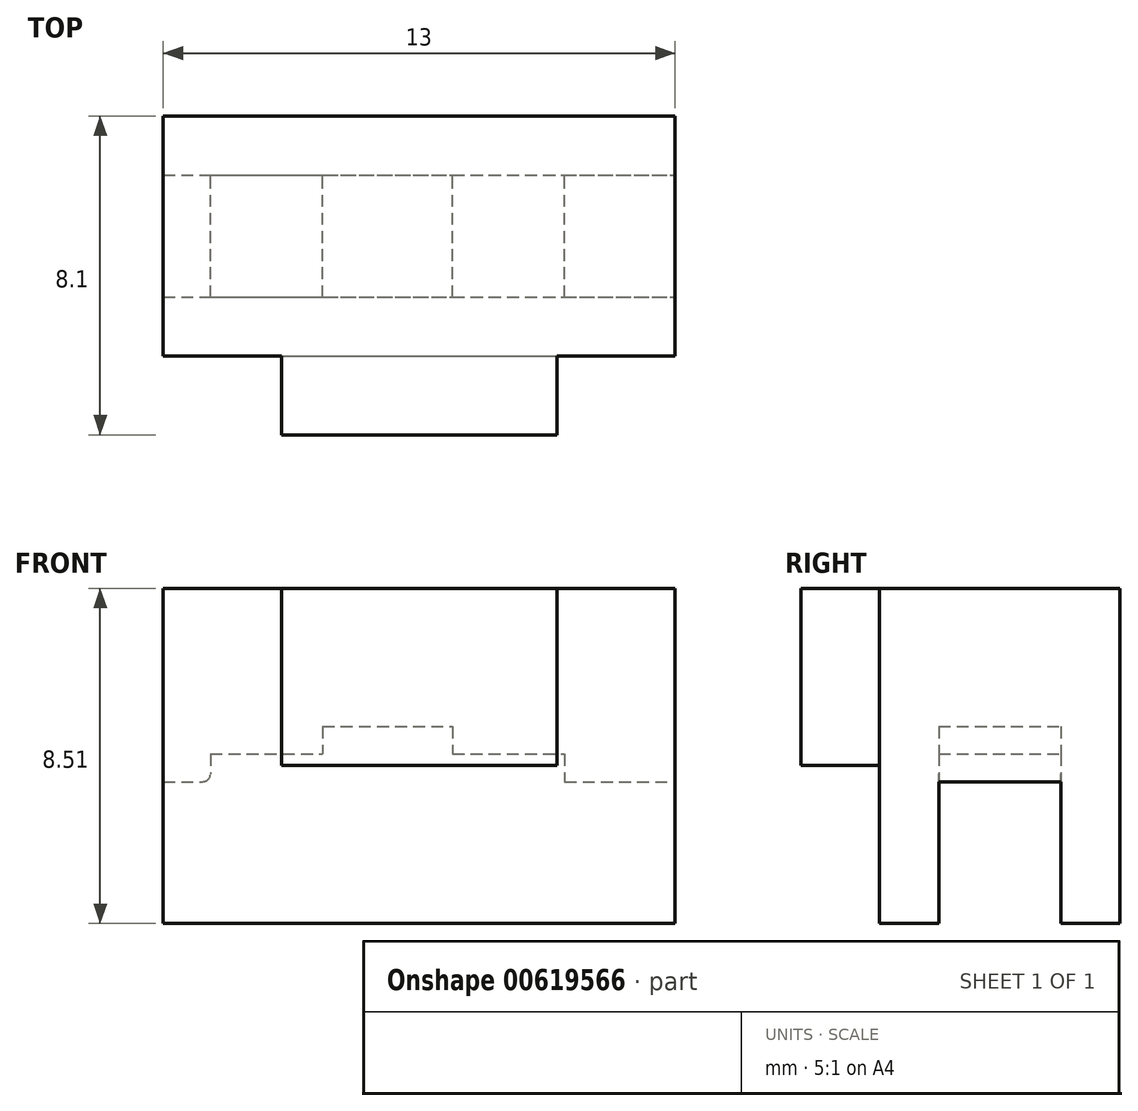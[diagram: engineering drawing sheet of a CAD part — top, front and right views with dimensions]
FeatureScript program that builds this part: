
annotation { "Feature Type Name" : "Feature", "Feature Type Description" : "" }
export const myFeature = defineFeature(function(context is Context, id is Id, definition is map)
    precondition{}
    {
        {
            var Q0;
            Q0=qCreatedBy(makeId("Top.planeOp"),FACE);
            var sketch = newSketch(context, id + "F0", { "sketchPlane" : qUnion([Q0])});
            skLineSegment(sketch, "E0.bottom", {"start": v(-6.5, 3.05) * mm, "end": v(6.5, 3.05) * mm});
            skLineSegment(sketch, "E0.top", {"start": v(-6.5, 1.55) * mm, "end": v(6.5, 1.55) * mm});
            skLineSegment(sketch, "E0.left", {"start": v(-6.5, 3.05) * mm, "end": v(-6.5, 1.55) * mm});
            skLineSegment(sketch, "E0.right", {"start": v(6.5, 3.05) * mm, "end": v(6.5, 1.55) * mm});
            skLineSegment(sketch, "E1.MirrorCS", {"start": v(6.5, -3.05) * mm, "end": v(6.5, -1.55) * mm});
            skLineSegment(sketch, "E2.MirrorCS", {"start": v(-6.5, -3.05) * mm, "end": v(-6.5, -1.55) * mm});
            skLineSegment(sketch, "E3.MirrorCS", {"start": v(-6.5, -3.05) * mm, "end": v(6.5, -3.05) * mm});
            skLineSegment(sketch, "E4.MirrorCS", {"start": v(-6.5, -1.55) * mm, "end": v(6.5, -1.55) * mm});
            skSolve(sketch);
        }
        {
            var Q0;
            Q0 = qSketchRegion(id + "F0", true);
            extrude(context, id + "F1", {"entities" : qUnion([Q0]), "oppositeDirection" : true, "depth" : 3.6 * mm, "offsetDistance" : 25 * mm});
        }
        {
            var Q0;
            Q0=qCreatedBy(makeId("Top.planeOp"),FACE);
            var sketch = newSketch(context, id + "F2", { "sketchPlane" : qUnion([Q0])});
            skLineSegment(sketch, "E5.bottom", {"start": v(-6.5, 3.05) * mm, "end": v(6.5, 3.05) * mm});
            skLineSegment(sketch, "E5.top", {"start": v(-6.5, -3.05) * mm, "end": v(6.5, -3.05) * mm});
            skLineSegment(sketch, "E5.left", {"start": v(-6.5, 3.05) * mm, "end": v(-6.5, -3.05) * mm});
            skLineSegment(sketch, "E5.right", {"start": v(6.5, 3.05) * mm, "end": v(6.5, -3.05) * mm});
            skSolve(sketch);
        }
        {
            var Q0;
            Q0 = qSketchRegion(id + "F2", true);
            extrude(context, id + "F3", {"entities" : qUnion([Q0]), "operationType" : NewBodyOperationType.ADD, "depth" : 4.9 * mm, "offsetDistance" : 25 * mm});
        }
        {
            var Q0;
            Q0=makeQuery(id+"F3.opExtrude","CAP_FACE",FACE,{"disambiguationData":[OSD([sQuery(id+"F2.wireOp",EDGE,"E5.bottom"),sQuery(id+"F2.wireOp",EDGE,"E5.top"),sQuery(id+"F2.wireOp",EDGE,"E5.left"),sQuery(id+"F2.wireOp",EDGE,"E5.right")])],"isStart":true});
            var sketch = newSketch(context, id + "F4", { "sketchPlane" : qUnion([Q0])});
            skLineSegment(sketch, "E6.bottom", {"start": v(-5.3, 1.55) * mm, "end": v(3.7, 1.55) * mm});
            skLineSegment(sketch, "E6.top", {"start": v(-5.3, -1.55) * mm, "end": v(3.7, -1.55) * mm});
            skLineSegment(sketch, "E6.left", {"start": v(-5.3, 1.55) * mm, "end": v(-5.3, -1.55) * mm});
            skLineSegment(sketch, "E6.right", {"start": v(3.7, 1.55) * mm, "end": v(3.7, -1.55) * mm});
            skSolve(sketch);
        }
        {
            var Q0;
            Q0=makeQuery(id+"F4.imprint","IMPRINT",FACE,{"disambiguationData":[TD([[makeQuery(id+"F4.imprint","IMPRINT",EDGE,{"derivedFrom":sQuery(id+"F4.wireOp",EDGE,"E6.bottom")}),-1.0]])]});
            extrude(context, id + "F5", {"entities" : qUnion([Q0]), "operationType" : NewBodyOperationType.REMOVE, "oppositeDirection" : true, "depth" : 0.7 * mm, "offsetDistance" : 25 * mm});
        }
        {
            var Q0;
            Q0=makeQuery(id+"F5.boolean.opBoolean","COPY",FACE,{"derivedFrom":makeQuery(id+"F5.opExtrude","CAP_FACE",FACE,{"disambiguationData":[OSD([sQuery(id+"F4.wireOp",EDGE,"E6.bottom"),sQuery(id+"F4.wireOp",EDGE,"E6.top"),sQuery(id+"F4.wireOp",EDGE,"E6.left"),sQuery(id+"F4.wireOp",EDGE,"E6.right")])],"isStart":false})});
            var sketch = newSketch(context, id + "F6", { "sketchPlane" : qUnion([Q0])});
            skLineSegment(sketch, "E7.bottom", {"start": v(-2.45, 1.55) * mm, "end": v(0.85, 1.55) * mm});
            skLineSegment(sketch, "E7.top", {"start": v(-2.45, -1.55) * mm, "end": v(0.85, -1.55) * mm});
            skLineSegment(sketch, "E7.left", {"start": v(-2.45, 1.55) * mm, "end": v(-2.45, -1.55) * mm});
            skLineSegment(sketch, "E7.right", {"start": v(0.85, 1.55) * mm, "end": v(0.85, -1.55) * mm});
            skSolve(sketch);
        }
        {
            var Q0;
            Q0=makeQuery(id+"F6.imprint","IMPRINT",FACE,{"disambiguationData":[TD([[makeQuery(id+"F6.imprint","IMPRINT",EDGE,{"derivedFrom":sQuery(id+"F6.wireOp",EDGE,"E7.bottom")}),-1.0]])]});
            extrude(context, id + "F7", {"entities" : qUnion([Q0]), "operationType" : NewBodyOperationType.REMOVE, "oppositeDirection" : true, "depth" : 0.7 * mm, "offsetDistance" : 25 * mm});
        }
        {
            var Q0;
            Q0=makeQuery(id+"F3.boolean.opBoolean","MERGE",FACE,{"derivedFrom":[makeQuery(id+"F1.opExtrude","SWEPT_FACE",FACE,{"disambiguationData":[OSD([sQuery(id+"F0.wireOp",EDGE,"E3.MirrorCS")])]}),makeQuery(id+"F3.opExtrude","SWEPT_FACE",FACE,{"disambiguationData":[OSD([sQuery(id+"F2.wireOp",EDGE,"E5.top")])]})]});
            var sketch = newSketch(context, id + "F8", { "sketchPlane" : qUnion([Q0])});
            skLineSegment(sketch, "E8.bottom", {"start": v(-3.5, 4.9) * mm, "end": v(3.5, 4.9) * mm});
            skLineSegment(sketch, "E8.top", {"start": v(-3.5, 0.4) * mm, "end": v(3.5, 0.4) * mm});
            skLineSegment(sketch, "E8.left", {"start": v(-3.5, 4.91) * mm, "end": v(-3.5, 0.4) * mm});
            skLineSegment(sketch, "E8.right", {"start": v(3.5, 4.91) * mm, "end": v(3.5, 0.4) * mm});
            skSolve(sketch);
        }
        {
            var Q0;
            Q0 = qSketchRegion(id + "F8", true);
            extrude(context, id + "F9", {"entities" : qUnion([Q0]), "operationType" : NewBodyOperationType.ADD, "depth" : 2 * mm, "offsetDistance" : 25 * mm});
        }
        {
            var Q0;
            Q0=makeQuery(id+"F5.boolean.opBoolean","COPY",EDGE,{"derivedFrom":makeQuery(id+"F5.opExtrude","CAP_EDGE",EDGE,{"disambiguationData":[OSD([sQuery(id+"F4.wireOp",EDGE,"E6.left")])],"isStart":true})});
            var Q1;
            Q1=makeQuery(id+"F5.boolean.opBoolean","COPY",EDGE,{"derivedFrom":makeQuery(id+"F5.opExtrude","CAP_EDGE",EDGE,{"disambiguationData":[OSD([sQuery(id+"F4.wireOp",EDGE,"E6.right")])],"isStart":true})});
            fillet(context, id + "F10", {"entities" : qUnion([Q0, Q1]), "radius" : 0.2 * mm, "tangentPropagation" : true, "allowEdgeOverflow" : false});
        }
    });
